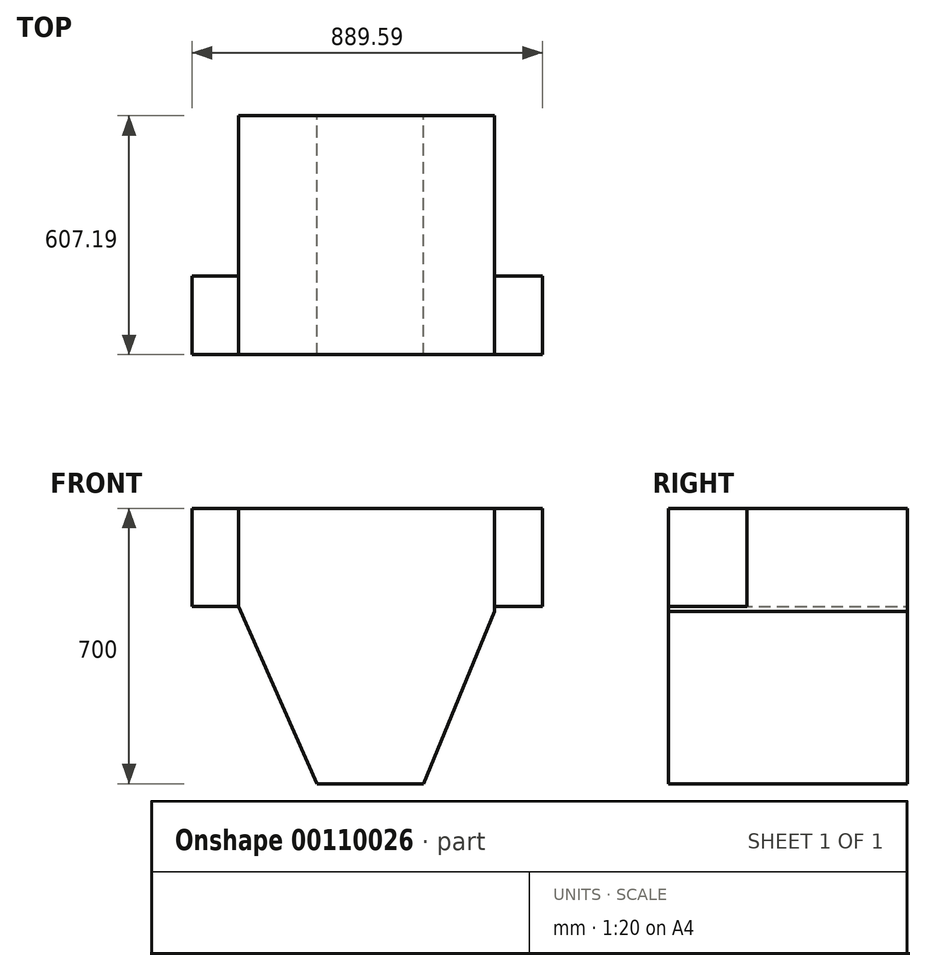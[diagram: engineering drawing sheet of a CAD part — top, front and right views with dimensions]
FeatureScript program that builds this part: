
annotation { "Feature Type Name" : "Feature", "Feature Type Description" : "" }
export const myFeature = defineFeature(function(context is Context, id is Id, definition is map)
    precondition{}
    {
        {
            var Q0;
            Q0=qCreatedBy(makeId("Front.planeOp"),FACE);
            var sketch = newSketch(context, id + "F0", { "sketchPlane" : qUnion([Q0])});
            skLineSegment(sketch, "E0.bottom", {"start": v(325, 350) * mm, "end": v(-325, 350) * mm});
            skLineSegment(sketch, "E0.top", {"start": v(144.53, -350) * mm, "end": v(-126.15, -350) * mm});
            skLineSegment(sketch, "E0.left", {"start": v(325, 350) * mm, "end": v(325, 88.25) * mm});
            skLineSegment(sketch, "E0.right", {"start": v(-325, 350) * mm, "end": v(-325, 100) * mm});
            skPoint(sketch, "E0.middle", {"position": v(0, 0) * mm});
            skLineSegment(sketch, "E1", {"start": v(-325, 100) * mm, "end": v(-126.15, -350) * mm});
            skLineSegment(sketch, "E2", {"start": v(-126.15, -350) * mm, "end": v(144.53, -350) * mm});
            skLineSegment(sketch, "E3", {"start": v(144.53, -350) * mm, "end": v(325, 88.25) * mm});
            skPoint(sketch, "E4.orphan", {"position": v(-325, -350) * mm});
            skPoint(sketch, "E5.orphan", {"position": v(325, -350) * mm});
            skSolve(sketch);
        }
        {
            var Q0;
            Q0=makeQuery(id+"F0.imprint","IMPRINT",FACE,{"disambiguationData":[TD([[makeQuery(id+"F0.imprint","IMPRINT",EDGE,{"derivedFrom":sQuery(id+"F0.wireOp",EDGE,"E0.bottom")}),1.0]])]});
            extrude(context, id + "F1", {"entities" : qUnion([Q0]), "depth" : 607.2 * mm});
        }
        {
            var Q0;
            Q0=makeQuery(id+"F1.opExtrude","CAP_FACE",FACE,{"disambiguationData":[OSD([sQuery(id+"F0.wireOp",EDGE,"E0.bottom"),sQuery(id+"F0.wireOp",EDGE,"E0.left"),sQuery(id+"F0.wireOp",EDGE,"E1"),sQuery(id+"F0.wireOp",EDGE,"E3"),sQuery(id+"F0.wireOp",EDGE,"E2"),sQuery(id+"F0.wireOp",EDGE,"E0.right")])],"isStart":false});
            var sketch = newSketch(context, id + "F2", { "sketchPlane" : qUnion([Q0])});
            skLineSegment(sketch, "E6.bottom", {"start": v(-325, 350) * mm, "end": v(-442.83, 350) * mm});
            skLineSegment(sketch, "E6.top", {"start": v(-325, 100) * mm, "end": v(-442.83, 100) * mm});
            skLineSegment(sketch, "E6.left", {"start": v(-325, 350) * mm, "end": v(-325, 100) * mm});
            skLineSegment(sketch, "E6.right", {"start": v(-442.83, 350) * mm, "end": v(-442.83, 100) * mm});
            skLineSegment(sketch, "E7.bottom", {"start": v(325, 350) * mm, "end": v(446.76, 350) * mm});
            skLineSegment(sketch, "E7.top", {"start": v(325, 100) * mm, "end": v(446.76, 100) * mm});
            skLineSegment(sketch, "E7.left", {"start": v(325, 350) * mm, "end": v(325, 100) * mm});
            skLineSegment(sketch, "E7.right", {"start": v(446.76, 350) * mm, "end": v(446.76, 100) * mm});
            skSolve(sketch);
        }
        {
            var Q0;
            Q0 = qSketchRegion(id + "F2", true);
            extrude(context, id + "F3", {"entities" : qUnion([Q0]), "oppositeDirection" : true, "depth" : 200 * mm});
        }
    });
